# Revit family: Faucet_Touchless-Lavatory-KOHLER-LOURE-K-98455T
name_source: partatom
category: Plumbing Fixtures
revit_build: Autodesk Revit 2017 (Build: 20160225_1515(x64)
units: mm (PartAtom-declared; Revit-internal decimal feet)

## family parameters
Cut with Voids When Loaded = No
Host = Face
OmniClass Number = 23.31.11.00
OmniClass Title = Faucets
Part Type = Normal
Room Calculation Point = No
Round Connector Dimension = Use Diameter
Shared = No

## types (2) — shared parameters
ADA Compliant = No
Assembly Code = D2010
CW Connection = Yes
Cold Water Inlet = Cold Water Inlet
Date Modified = 12/24/2020
Default Elevation = 36"
Drain Included = Yes
Finish = Kohler-Metal-CP-Polished_Chrome
Flow Rate = 1 GPM
HW Connection = No
Height = 8 1/16"
Hot Water Inlet = Hot Water Inlet
Length = 4"
Manufacturer = KOHLER Co.
Master Format 2014 = 22 41 39
Master Format 2014 Name = Residential Faucets, Supplies, and Trim
Material = Premium Metal construction
Pressure = 43.50 psi
Product Name = LOURE
Spout Reach = 4"
URL = https://www.kohler.com.cn
Vent Connection = No
Waste Connection = No
Waste Water Outlet = Waste Water Outlet
WaterSense Certified = No
Width = 2 7/16"

## per-type parameters (varying)
| type | Description | Model | Product Documentation Link | Product Page URL | Type |
| B, CP-Polished Chrome | Basin induction faucet-DC (single cooling type) | K-98455T-B-CP | https://files.kohler.com.cn | https://www.kohler.com.cn | 1 |
| CP-Polished Chrome | DECK MOUNT SENSOR FAUCET-DC | K-98455T-CP |  |  | 2 |

## geometry (parser evidence)
native form markers: Sweep x5
no freeform markers — native parametric forms only
